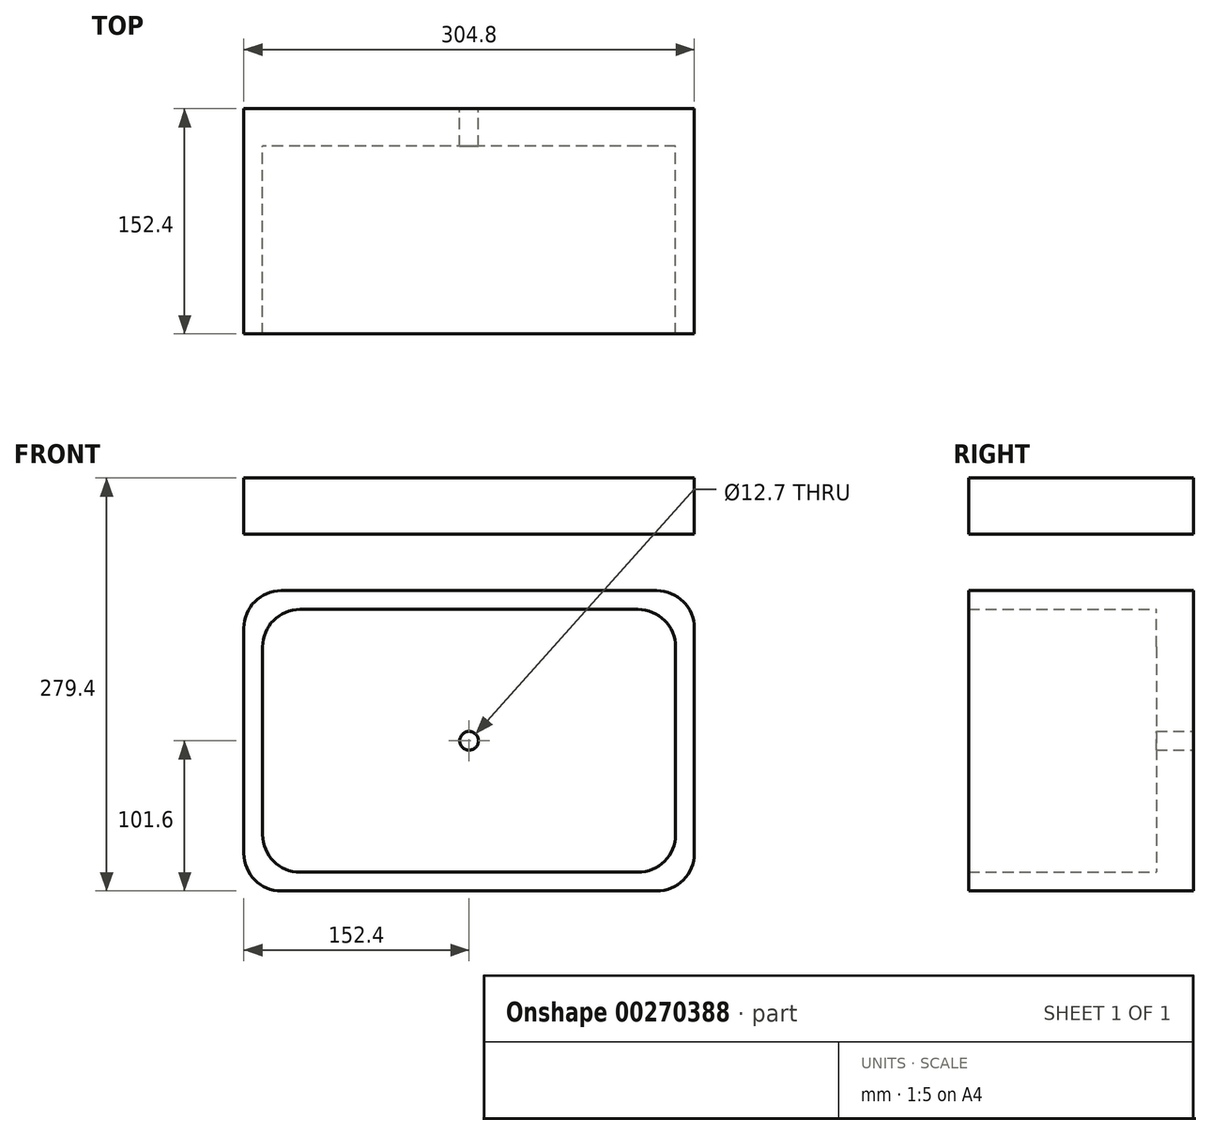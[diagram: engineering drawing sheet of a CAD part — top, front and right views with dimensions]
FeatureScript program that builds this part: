
annotation { "Feature Type Name" : "Feature", "Feature Type Description" : "" }
export const myFeature = defineFeature(function(context is Context, id is Id, definition is map)
    precondition{}
    {
        {
            var Q0;
            Q0=qCreatedBy(makeId("Front.planeOp"),FACE);
            var sketch = newSketch(context, id + "F0", { "sketchPlane" : qUnion([Q0])});
            skLineSegment(sketch, "E0.bottom", {"start": v(152.4, 101.6) * mm, "end": v(-152.4, 101.6) * mm});
            skLineSegment(sketch, "E0.top", {"start": v(127, -101.6) * mm, "end": v(-127, -101.6) * mm});
            skLineSegment(sketch, "E0.left", {"start": v(152.4, 76.2) * mm, "end": v(152.4, -76.2) * mm});
            skLineSegment(sketch, "E0.right", {"start": v(-152.4, 76.2) * mm, "end": v(-152.4, -76.2) * mm});
            skPoint(sketch, "E0.middle", {"position": v(0, 0) * mm});
            skLineSegment(sketch, "E1.bottom", {"start": v(-127, 101.6) * mm, "end": v(127, 101.6) * mm});
            skLineSegment(sketch, "E1.top", {"start": v(-152.4, 177.8) * mm, "end": v(152.4, 177.8) * mm});
            skLineSegment(sketch, "E1.left", {"start": v(-152.4, 101.6) * mm, "end": v(-152.4, 177.8) * mm});
            skLineSegment(sketch, "E1.right", {"start": v(152.4, 101.6) * mm, "end": v(152.4, 177.8) * mm});
            skPoint(sketch, "E2.visualSharp", {"position": v(-152.4, 101.6) * mm});
            skArc(sketch, "E2.filletArc", {"start": v(-127, 101.6) * mm, "mid": v(-144.96, 94.16) * mm, "end": v(-152.4, 76.2) * mm});
            skPoint(sketch, "E3.visualSharp", {"position": v(-152.4, -101.6) * mm});
            skArc(sketch, "E3.filletArc", {"start": v(-152.4, -76.2) * mm, "mid": v(-144.96, -94.16) * mm, "end": v(-127, -101.6) * mm});
            skPoint(sketch, "E4.visualSharp", {"position": v(152.4, -101.6) * mm});
            skArc(sketch, "E4.filletArc", {"start": v(127, -101.6) * mm, "mid": v(144.96, -94.16) * mm, "end": v(152.4, -76.2) * mm});
            skPoint(sketch, "E5.visualSharp", {"position": v(152.4, 101.6) * mm});
            skArc(sketch, "E5.filletArc", {"start": v(152.4, 76.2) * mm, "mid": v(144.96, 94.16) * mm, "end": v(127, 101.6) * mm});
            skLineSegment(sketch, "E6.bottom", {"start": v(139.7, 88.9) * mm, "end": v(-139.7, 88.9) * mm});
            skLineSegment(sketch, "E6.top", {"start": v(114.3, -88.9) * mm, "end": v(-114.3, -88.9) * mm});
            skLineSegment(sketch, "E6.left", {"start": v(139.7, 63.5) * mm, "end": v(139.7, -63.5) * mm});
            skLineSegment(sketch, "E6.right", {"start": v(-139.7, 63.5) * mm, "end": v(-139.7, -63.5) * mm});
            skLineSegment(sketch, "E7.bottom", {"start": v(-114.3, 88.9) * mm, "end": v(114.3, 88.9) * mm});
            skPoint(sketch, "E8.visualSharp", {"position": v(-139.7, 88.9) * mm});
            skArc(sketch, "E8.filletArc", {"start": v(-114.3, 88.9) * mm, "mid": v(-132.26, 81.46) * mm, "end": v(-139.7, 63.5) * mm});
            skPoint(sketch, "E9.visualSharp", {"position": v(-139.7, -88.9) * mm});
            skArc(sketch, "E9.filletArc", {"start": v(-139.7, -63.5) * mm, "mid": v(-132.26, -81.46) * mm, "end": v(-114.3, -88.9) * mm});
            skPoint(sketch, "E10.visualSharp", {"position": v(139.7, -88.9) * mm});
            skArc(sketch, "E10.filletArc", {"start": v(114.3, -88.9) * mm, "mid": v(132.26, -81.46) * mm, "end": v(139.7, -63.5) * mm});
            skPoint(sketch, "E11.visualSharp", {"position": v(139.7, 88.9) * mm});
            skArc(sketch, "E11.filletArc", {"start": v(139.7, 63.5) * mm, "mid": v(132.26, 81.46) * mm, "end": v(114.3, 88.9) * mm});
            skCircle(sketch, "E12", {"center": v(0, 0) * mm, "radius": 6.35 * mm});
            skLineSegment(sketch, "E13", {"start": v(-152.4, 139.7) * mm, "end": v(152.4, 139.7) * mm});
            skLineSegment(sketch, "E14", {"start": v(0, 177.8) * mm, "end": v(0, 101.6) * mm});
            skPoint(sketch, "E15", {"position": v(-76.2, 139.7) * mm});
            skPoint(sketch, "E16", {"position": v(76.2, 139.7) * mm});
            skPoint(sketch, "E17", {"position": v(0, 139.7) * mm});
            skSolve(sketch);
        }
        {
            var Q0;
            Q0=makeQuery(id+"F0.imprint","IMPRINT",FACE,{"disambiguationData":[TD([[makeQuery(id+"F0.imprint","IMPRINT",EDGE,{"derivedFrom":sQuery(id+"F0.wireOp",EDGE,"E6.top")}),-1.0]])]});
            extrude(context, id + "F1", {"entities" : qUnion([Q0]), "depth" : 25.4 * mm});
        }
        {
            var Q0;
            Q0=makeQuery(id+"F0.imprint","IMPRINT",FACE,{"disambiguationData":[TD([[makeQuery(id+"F0.imprint","IMPRINT",EDGE,{"derivedFrom":sQuery(id+"F0.wireOp",EDGE,"E0.top")}),-1.0]])]});
            extrude(context, id + "F2", {"entities" : qUnion([Q0]), "operationType" : NewBodyOperationType.ADD, "depth" : 152.4 * mm});
        }
        {
            var Q0;
            {var subQ0=sQuery(id+"F0.wireOp",EDGE,"E1.bottom");Q0=makeQuery(id+"F0.imprint","IMPRINT",FACE,{"disambiguationData":[TD([[makeQuery(id+"F0.imprint","IMPRINT",EDGE,{"derivedFrom":subQ0}),1.0]])]});}
            var Q1;
            {var subQ0=sQuery(id+"F0.wireOp",EDGE,"E1.left");var subQ1=sQuery(id+"F0.wireOp",EDGE,"E1.top");var subQ2=makeQuery(id+"F0.imprint","INTERSECT",VERTEX,{"derivedFrom":[subQ1,subQ0]});Q1=makeQuery(id+"F0.imprint","IMPRINT",FACE,{"disambiguationData":[TD([[makeQuery(id+"F0.imprint","IMPRINT",EDGE,{"disambiguationData":[TD([[subQ2,-1.0]])],"derivedFrom":subQ1}),-1.0]])]});}
            var Q2;
            {var subQ0=sQuery(id+"F0.wireOp",EDGE,"E1.right");var subQ1=sQuery(id+"F0.wireOp",EDGE,"E1.top");var subQ2=makeQuery(id+"F0.imprint","INTERSECT",VERTEX,{"derivedFrom":[subQ1,subQ0]});Q2=makeQuery(id+"F0.imprint","IMPRINT",FACE,{"disambiguationData":[TD([[makeQuery(id+"F0.imprint","IMPRINT",EDGE,{"disambiguationData":[TD([[subQ2,1.0]])],"derivedFrom":subQ1}),-1.0]])]});}
            extrude(context, id + "F3", {"entities" : qUnion([Q0, Q1, Q2]), "operationType" : NewBodyOperationType.ADD, "depth" : 152.4 * mm});
        }
    });
